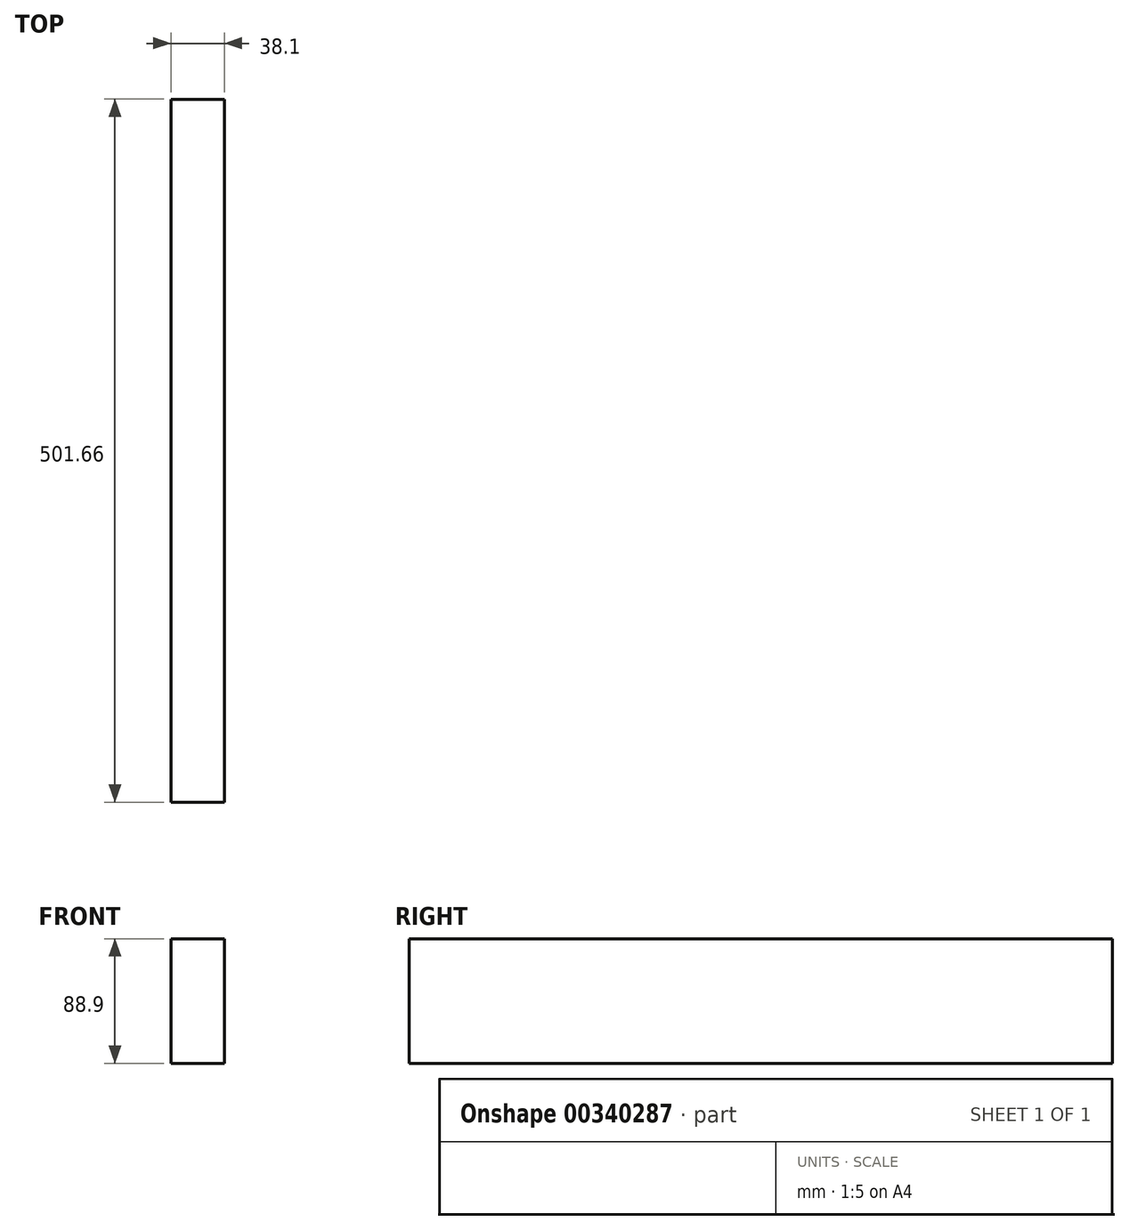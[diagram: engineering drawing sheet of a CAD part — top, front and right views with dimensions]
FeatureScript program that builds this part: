
annotation { "Feature Type Name" : "Feature", "Feature Type Description" : "" }
export const myFeature = defineFeature(function(context is Context, id is Id, definition is map)
    precondition{}
    {
        {
            var Q0;
            Q0=qCreatedBy(makeId("Front.planeOp"),FACE);
            var sketch = newSketch(context, id + "F0", { "sketchPlane" : qUnion([Q0])});
            skLineSegment(sketch, "E0.bottom", {"start": v(19.05, -44.45) * mm, "end": v(-19.05, -44.45) * mm});
            skLineSegment(sketch, "E0.top", {"start": v(19.05, 44.45) * mm, "end": v(-19.05, 44.45) * mm});
            skLineSegment(sketch, "E0.left", {"start": v(19.05, -44.45) * mm, "end": v(19.05, 44.45) * mm});
            skLineSegment(sketch, "E0.right", {"start": v(-19.05, -44.45) * mm, "end": v(-19.05, 44.45) * mm});
            skPoint(sketch, "E0.middle", {"position": v(0, 0) * mm});
            skSolve(sketch);
        }
        {
            var Q0;
            Q0=qSketchRegion(id+"F0",true);
            extrude(context, id + "F1", {"entities" : qUnion([Q0]), "endBound" : BoundingType.SYMMETRIC, "depth" : 501.65 * mm});
        }
    });
